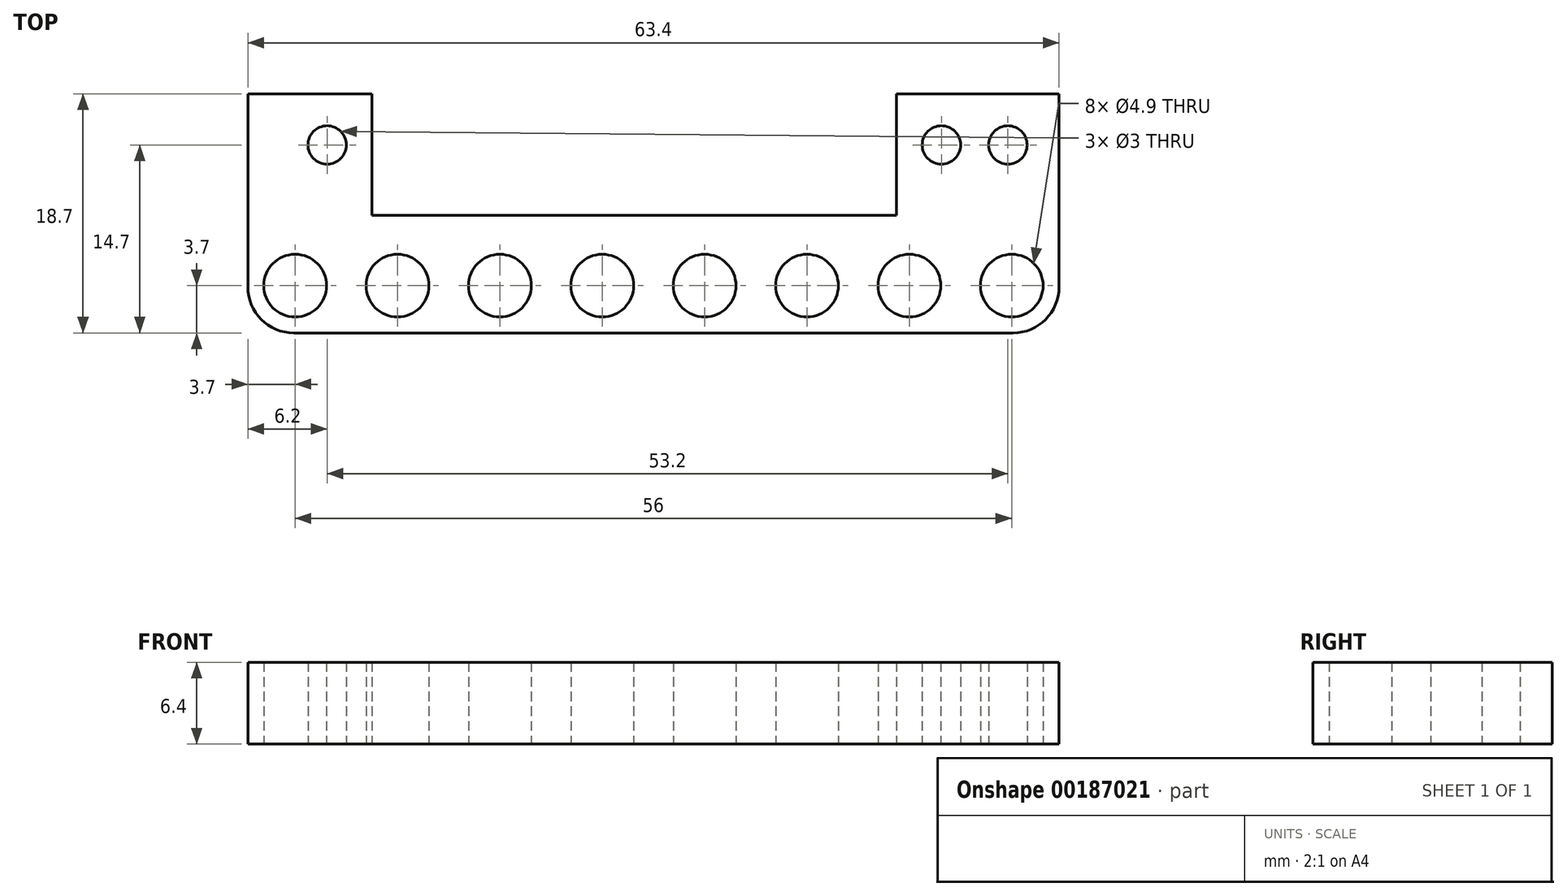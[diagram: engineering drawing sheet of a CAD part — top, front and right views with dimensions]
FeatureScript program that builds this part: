
annotation { "Feature Type Name" : "Feature", "Feature Type Description" : "" }
export const myFeature = defineFeature(function(context is Context, id is Id, definition is map)
    precondition{}
    {
        {
            var Q0;
            Q0=qCreatedBy(makeId("Top.planeOp"),FACE);
            var sketch = newSketch(context, id + "F0", { "sketchPlane" : qUnion([Q0])});
            skLineSegment(sketch, "E0", {"start": v(-31.7, 18.7) * mm, "end": v(-22, 18.7) * mm});
            skLineSegment(sketch, "E1", {"start": v(-22, 18.7) * mm, "end": v(-22, 9.2) * mm});
            skLineSegment(sketch, "E2", {"start": v(-22, 9.2) * mm, "end": v(19, 9.2) * mm});
            skLineSegment(sketch, "E3", {"start": v(19, 9.2) * mm, "end": v(19, 18.7) * mm});
            skLineSegment(sketch, "E4", {"start": v(19, 18.7) * mm, "end": v(31.7, 18.7) * mm});
            skLineSegment(sketch, "E5", {"start": v(31.7, 18.7) * mm, "end": v(31.7, 0) * mm});
            skLineSegment(sketch, "E6", {"start": v(31.7, 0) * mm, "end": v(-31.7, 0) * mm});
            skLineSegment(sketch, "E7", {"start": v(-31.7, 0) * mm, "end": v(-31.7, 18.7) * mm});
            skCircle(sketch, "E8", {"center": v(-25.5, 14.7) * mm, "radius": 1.5 * mm});
            skCircle(sketch, "E9", {"center": v(22.5, 14.7) * mm, "radius": 1.5 * mm});
            skCircle(sketch, "E10", {"center": v(-28, 3.7) * mm, "radius": 2.45 * mm});
            skCircle(sketch, "E11", {"center": v(4, 3.7) * mm, "radius": 2.45 * mm});
            skCircle(sketch, "E12", {"center": v(-12, 3.7) * mm, "radius": 2.45 * mm});
            skCircle(sketch, "E13", {"center": v(-4, 3.7) * mm, "radius": 2.45 * mm});
            skLineSegment(sketch, "E14.top", {"start": v(-10.35, 0) * mm, "end": v(-18.35, 0) * mm});
            skCircle(sketch, "E15", {"center": v(-20, 3.7) * mm, "radius": 2.45 * mm});
            skCircle(sketch, "E16", {"center": v(12, 3.7) * mm, "radius": 2.45 * mm});
            skCircle(sketch, "E17", {"center": v(20, 3.7) * mm, "radius": 2.45 * mm});
            skCircle(sketch, "E18", {"center": v(28, 3.7) * mm, "radius": 2.45 * mm});
            skCircle(sketch, "E19", {"center": v(27.7, 14.7) * mm, "radius": 1.5 * mm});
            skSolve(sketch);
        }
        {
            var Q0;
            Q0=makeQuery(id+"F0.imprint","IMPRINT",FACE,{"disambiguationData":[TD([[makeQuery(id+"F0.imprint","IMPRINT",EDGE,{"derivedFrom":sQuery(id+"F0.wireOp",EDGE,"E0")}),-1.0]])]});
            extrude(context, id + "F1", {"entities" : qUnion([Q0]), "depth" : 6.4 * mm});
        }
        {
            var Q0;
            Q0=makeQuery(id+"F1.opExtrude","SWEPT_EDGE",EDGE,{"disambiguationData":[OSD([sQuery(id+"F0.wireOp",EDGE,"E6"),sQuery(id+"F0.wireOp",EDGE,"E7")])]});
            var Q1;
            Q1=makeQuery(id+"F1.opExtrude","SWEPT_EDGE",EDGE,{"disambiguationData":[OSD([sQuery(id+"F0.wireOp",EDGE,"E5"),sQuery(id+"F0.wireOp",EDGE,"E6")])]});
            fillet(context, id + "F2", {"entities" : qUnion([Q0, Q1]), "radius" : 3.6 * mm, "tangentPropagation" : true, "allowEdgeOverflow" : false});
        }
    });
